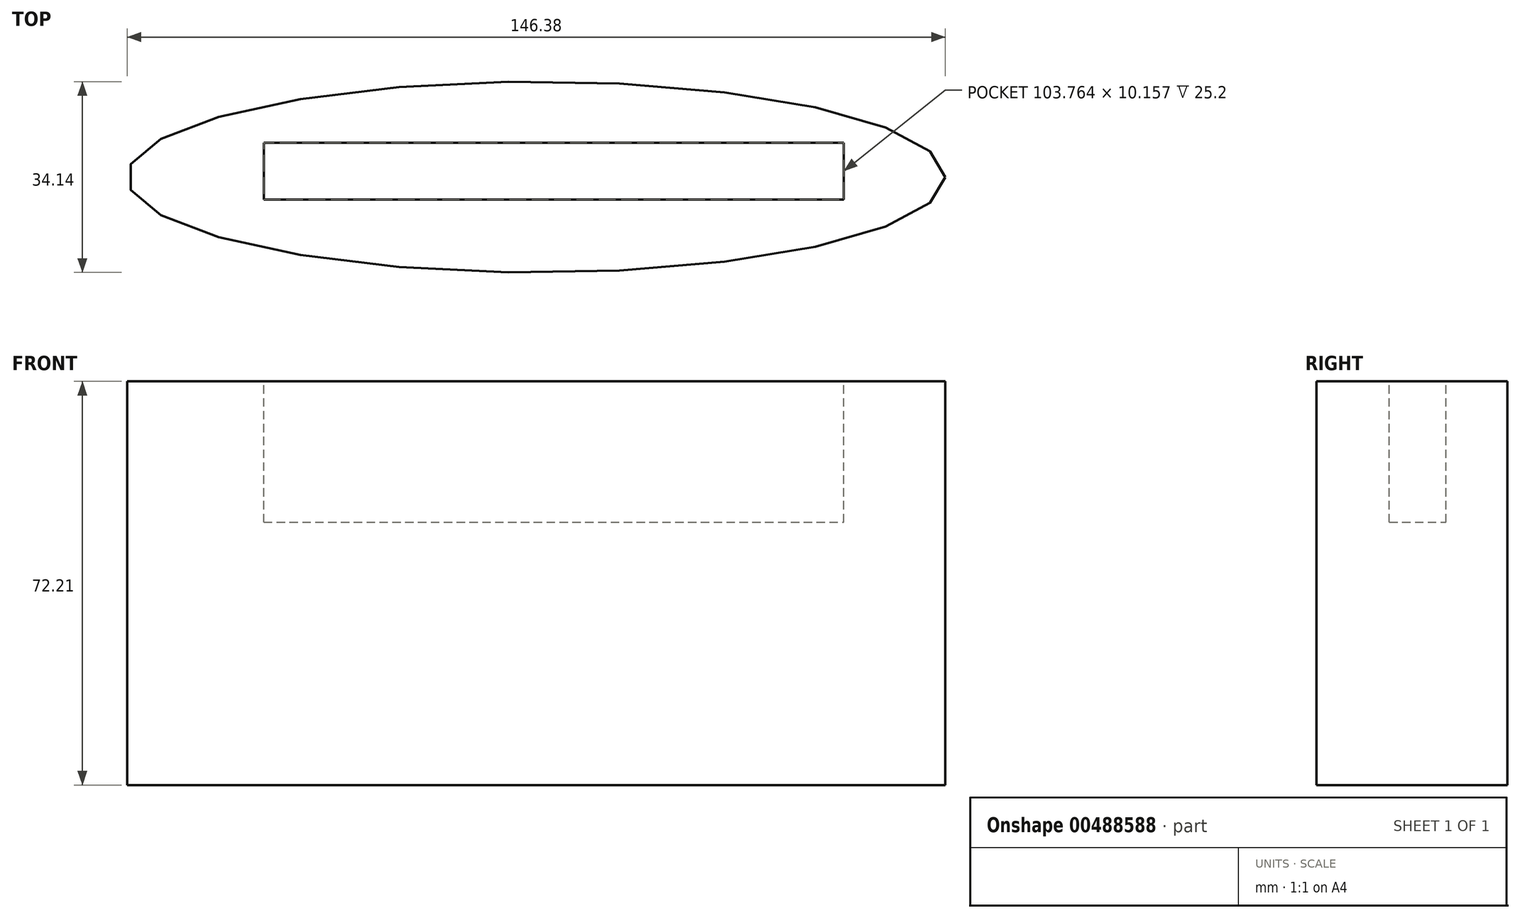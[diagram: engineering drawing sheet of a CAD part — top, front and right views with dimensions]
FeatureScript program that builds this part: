
annotation { "Feature Type Name" : "Feature", "Feature Type Description" : "" }
export const myFeature = defineFeature(function(context is Context, id is Id, definition is map)
    precondition{}
    {
        {
            var Q0;
            Q0=qCreatedBy(makeId("Top.planeOp"),FACE);
            var sketch = newSketch(context, id + "F0", { "sketchPlane" : qUnion([Q0])});
            skEllipse(sketch, "E0", {"center": v(-51.2, 16.25) * mm, "majorRadius": 73.19 * mm, "minorRadius": 17.07 * mm, "majorAxis": v(1, 0)});
            skSolve(sketch);
        }
        {
            var Q0;
            Q0 = qSketchRegion(id + "F0", true);
            extrude(context, id + "F1", {"entities" : qUnion([Q0]), "depth" : 72.2 * mm});
        }
        {
            var Q0;
            Q0=makeQuery(id+"F1.opExtrude","CAP_FACE",FACE,{"disambiguationData":[OSD([sQuery(id+"F0.wireOp",EDGE,"E0")])],"isStart":false});
            var sketch = newSketch(context, id + "F2", { "sketchPlane" : qUnion([Q0])});
            skSolve(sketch);
        }
        {
            var Q0;
            Q0=makeQuery(id+"F2.imprint","IMPRINT",FACE,{"disambiguationData":[TD([[makeQuery(id+"F2.imprint","IMPRINT",EDGE,{"derivedFrom":makeQuery(id+"F1.opExtrude","CAP_EDGE",EDGE,{"disambiguationData":[OSD([sQuery(id+"F0.wireOp",EDGE,"E0")])],"isStart":false})}),1.0]])]});
            var sketch = newSketch(context, id + "F3", { "sketchPlane" : qUnion([Q0])});
            skLineSegment(sketch, "E1.bottom", {"start": v(-99.93, 12.2) * mm, "end": v(3.83, 12.2) * mm});
            skLineSegment(sketch, "E1.top", {"start": v(-99.93, 22.36) * mm, "end": v(3.83, 22.36) * mm});
            skLineSegment(sketch, "E1.left", {"start": v(-99.93, 12.2) * mm, "end": v(-99.93, 22.36) * mm});
            skLineSegment(sketch, "E1.right", {"start": v(3.83, 12.2) * mm, "end": v(3.83, 22.36) * mm});
            skPoint(sketch, "E1.middle", {"position": v(-48.05, 17.28) * mm});
            skSolve(sketch);
        }
        {
            var Q0;
            Q0 = qSketchRegion(id + "F3", true);
            extrude(context, id + "F4", {"entities" : qUnion([Q0]), "operationType" : NewBodyOperationType.REMOVE, "oppositeDirection" : true, "depth" : 25.2 * mm});
        }
    });
